# Revit family: Gelenkhalter mit Anschlusslochung M8-M12 zu M8-M12 VA
name_source: partatom
category: HLS-Bauteile
revit_build: Autodesk Revit 2017 (Build: 20190508_0315(x64)
units: mm (PartAtom-declared; Revit-internal decimal feet)

## family parameters
Arbeitsebenenbasiert = Ja
Beim Laden mit Abzugskörper schneiden = Nein
Bemaßung runder Anschluss = Durchmesser verwenden
Gemeinsam genutzt = Ja
Immer vertikal = Nein
Raumberechnungspunkt = Nein
Teiletyp = Normal

## types (2) — shared parameters
Anschluss B1 = M8-M12
Anschluss B2 = M8-M12
Anschlusslochung B1 = 13 mm
Anschlusslochung B2 = 13 mm
Fabrikat = MEFA
Gewicht = 0.67 kg
Gewicht pro Bauteil = 0.67 kg
Kurztext2 = Anschlusslöcher für M8-M12 & M8-M12
Lochdurchmesser = 13 mm
Material = Stahl
Mengeneinheit = St
Oberflaeche = galvanisch verzinkt
Profil = C-Profil
Profiltyp = 45
Vorgabe-Ansicht = 1219 mm
Winkel = 90 °
max. zul. Last = 10.00 kN
vpe = 1

## per-type parameters (varying)
| type | Artikelnummer | EAN | Kurztext1 | Materialname |
| Gelenkhalter mit Anschlusslochung M8-M12/M8-M12 V4A | 0481207 | 4250928412881 | Gelenkhalter Anschlussloch V4A | V4A |
| Gelenkhalter mit Anschlusslochung M8-M12/M8-M12 V2A | 0480207 | 4250928412560 | Gelenkhalter Anschlussloch V2A | V2A |

## geometry (parser evidence)
native form markers: Sweep x3
no freeform markers — native parametric forms only
